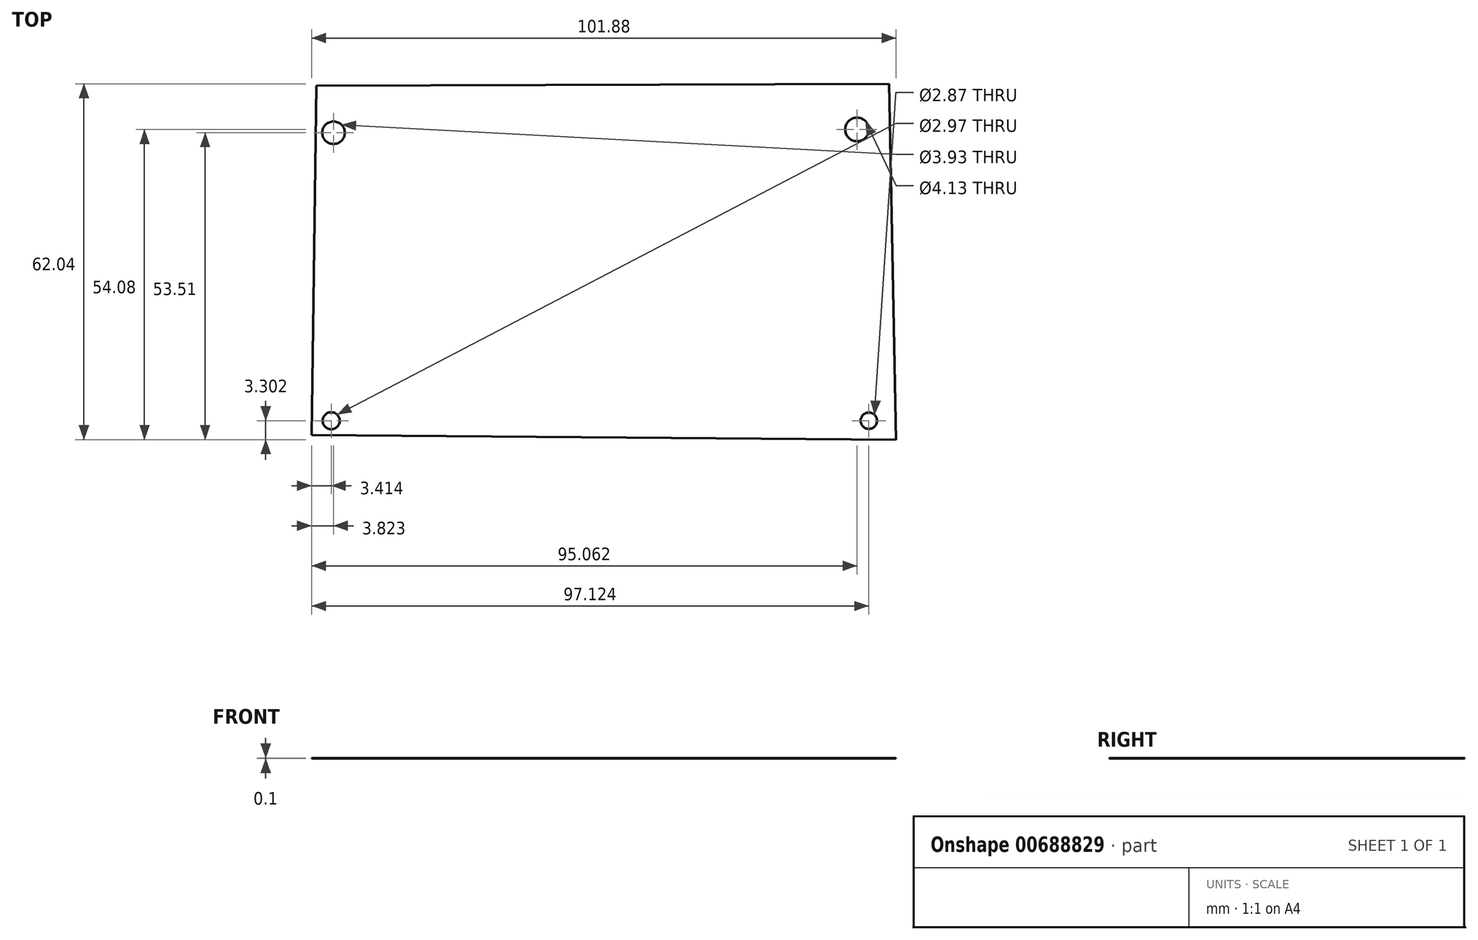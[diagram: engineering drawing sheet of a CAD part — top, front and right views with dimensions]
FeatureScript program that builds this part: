
annotation { "Feature Type Name" : "Feature", "Feature Type Description" : "" }
export const myFeature = defineFeature(function(context is Context, id is Id, definition is map)
    precondition{}
    {
        {
            var Q0;
            Q0=qCreatedBy(makeId("Top.planeOp"),FACE);
            var sketch = newSketch(context, id + "F0", { "sketchPlane" : qUnion([Q0])});
            skCircle(sketch, "E0", {"center": v(-54.34, 24.76) * mm, "radius": 1.97 * mm});
            skPoint(sketch, "E0.first.point", {"position": v(-55.78, 26.1) * mm});
            skPoint(sketch, "E0.second.point", {"position": v(-52.76, 25.93) * mm});
            skPoint(sketch, "E0.third.point", {"position": v(-55, 22.9) * mm});
            skCircle(sketch, "E1", {"center": v(-54.75, -25.45) * mm, "radius": 1.48 * mm});
            skPoint(sketch, "E1.first.point", {"position": v(-55.68, -24.3) * mm});
            skPoint(sketch, "E1.second.point", {"position": v(-53.27, -25.3) * mm});
            skPoint(sketch, "E1.third.point", {"position": v(-54.85, -26.93) * mm});
            skCircle(sketch, "E2", {"center": v(38.96, -25.45) * mm, "radius": 1.43 * mm});
            skPoint(sketch, "E2.first.point", {"position": v(38.01, -24.38) * mm});
            skPoint(sketch, "E2.second.point", {"position": v(40.38, -25.24) * mm});
            skPoint(sketch, "E2.third.point", {"position": v(38.75, -26.86) * mm});
            skCircle(sketch, "E3", {"center": v(36.9, 25.33) * mm, "radius": 2.06 * mm});
            skPoint(sketch, "E3.first.point", {"position": v(35.99, 27.18) * mm});
            skPoint(sketch, "E3.second.point", {"position": v(38.96, 25.26) * mm});
            skPoint(sketch, "E3.third.point", {"position": v(35.86, 23.55) * mm});
            skLineSegment(sketch, "E4", {"start": v(36.9, 25.33) * mm, "end": v(-54.34, 24.76) * mm, "construction": true});
            skLineSegment(sketch, "E5", {"start": v(-54.34, 24.76) * mm, "end": v(-54.75, -25.45) * mm, "construction": true});
            skLineSegment(sketch, "E6", {"start": v(-54.75, -25.45) * mm, "end": v(38.96, -25.45) * mm, "construction": true});
            skLineSegment(sketch, "E7", {"start": v(38.96, -25.45) * mm, "end": v(36.9, 25.33) * mm, "construction": true});
            skLineSegment(sketch, "E8", {"start": v(37.93, -0.06) * mm, "end": v(-8.3, -0.2) * mm, "construction": true});
            skLineSegment(sketch, "E9", {"start": v(-8.3, -0.2) * mm, "end": v(-54.54, -0.34) * mm, "construction": true});
            skLineSegment(sketch, "E10", {"start": v(-57.3, 32.98) * mm, "end": v(42.5, 33.29) * mm});
            skLineSegment(sketch, "E11", {"start": v(42.5, 33.29) * mm, "end": v(43.72, -28.75) * mm});
            skLineSegment(sketch, "E12", {"start": v(43.72, -28.75) * mm, "end": v(-58.16, -27.94) * mm});
            skLineSegment(sketch, "E13", {"start": v(-58.16, -27.94) * mm, "end": v(-57.3, 32.98) * mm});
            skSolve(sketch);
        }
        {
            var Q0;
            Q0 = qSketchRegion(id + "F0", true);
            var Q1;
            Q1=sQuery(id+"F0.wireOp",EDGE,"E13");
            var Q2;
            Q2=sQuery(id+"F0.wireOp",EDGE,"E10");
            var Q3;
            Q3=sQuery(id+"F0.wireOp",EDGE,"E11");
            var Q4;
            Q4=sQuery(id+"F0.wireOp",EDGE,"E12");
            extrude(context, id + "F1", {"entities" : qUnion([Q0]), "surfaceEntities" : qUnion([Q1, Q2, Q3, Q4]), "depth" : 0.1 * mm, "offsetDistance" : 25 * mm});
        }
    });
